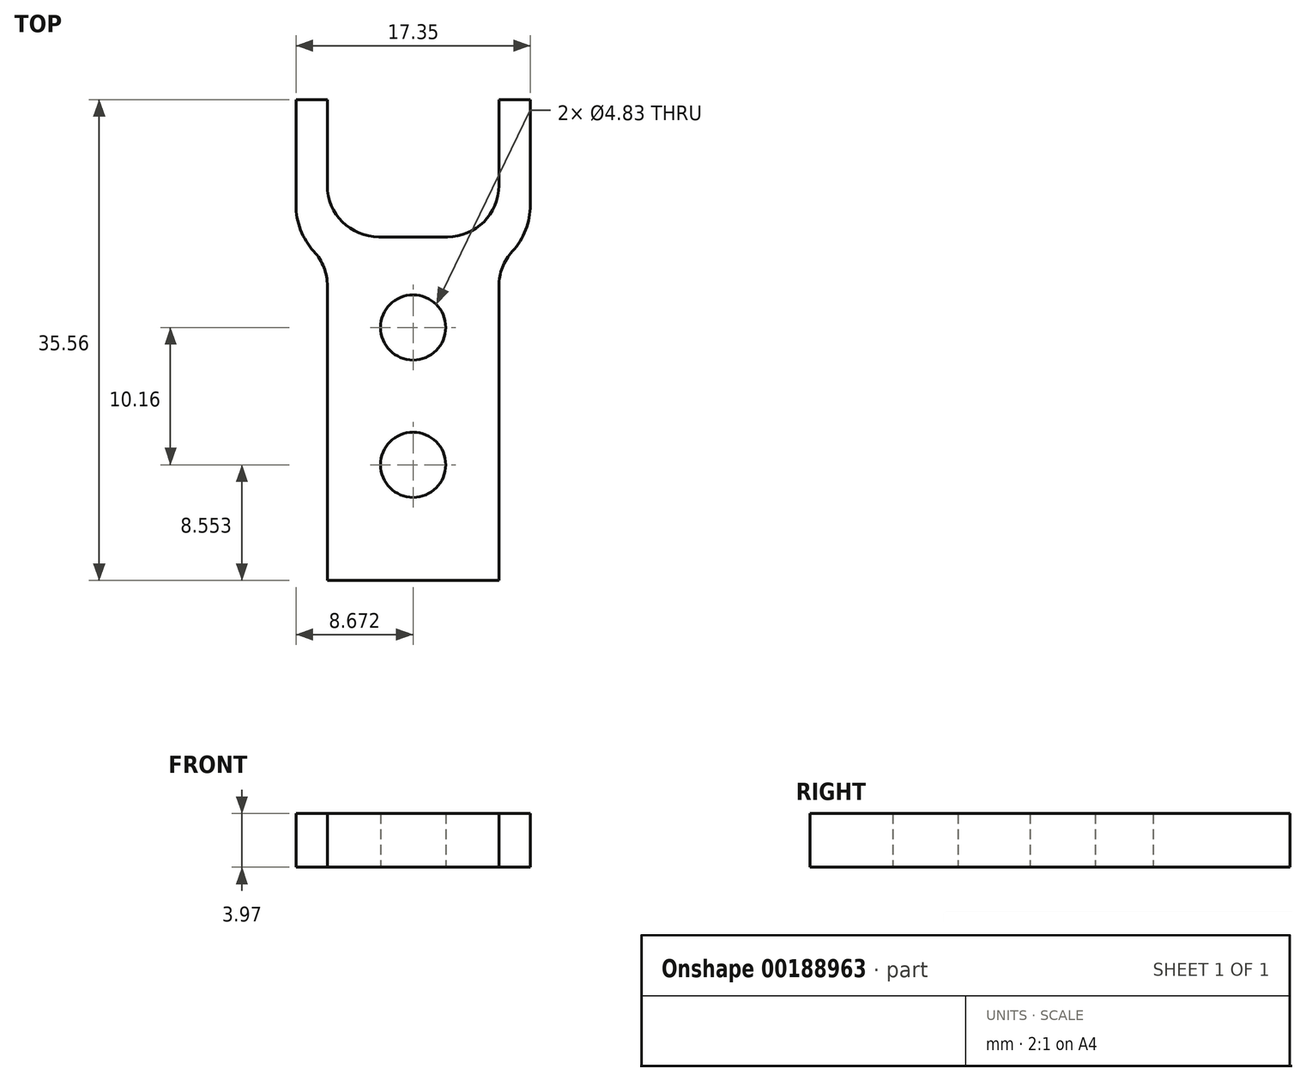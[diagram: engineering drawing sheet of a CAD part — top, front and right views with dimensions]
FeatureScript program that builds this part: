
annotation { "Feature Type Name" : "Feature", "Feature Type Description" : "" }
export const myFeature = defineFeature(function(context is Context, id is Id, definition is map)
    precondition{}
    {
        {
            var Q0;
            Q0=qCreatedBy(makeId("Top.planeOp"),FACE);
            var sketch = newSketch(context, id + "F0", { "sketchPlane" : qUnion([Q0])});
            skCircle(sketch, "E0", {"center": v(-68.64, 47.74) * mm, "radius": 6.88 * mm, "construction": true});
            skLineSegment(sketch, "E1", {"start": v(-68.64, 54.62) * mm, "end": v(-75.52, 47.74) * mm, "construction": true});
            skLineSegment(sketch, "E2", {"start": v(-75.52, 47.74) * mm, "end": v(-75.52, 54.62) * mm, "construction": true});
            skLineSegment(sketch, "E3", {"start": v(-75.52, 54.62) * mm, "end": v(-68.64, 54.62) * mm, "construction": true});
            skLineSegment(sketch, "E4", {"start": v(-68.64, 54.62) * mm, "end": v(-61.77, 47.74) * mm, "construction": true});
            skLineSegment(sketch, "E5", {"start": v(-61.77, 47.74) * mm, "end": v(-61.77, 54.62) * mm, "construction": true});
            skLineSegment(sketch, "E6", {"start": v(-61.77, 54.62) * mm, "end": v(-68.64, 54.62) * mm, "construction": true});
            skLineSegment(sketch, "E7.bottom", {"start": v(-75.88, 33.2) * mm, "end": v(-63.18, 33.2) * mm});
            skLineSegment(sketch, "E7.top", {"start": v(-75.88, 7.8) * mm, "end": v(-63.18, 7.8) * mm});
            skLineSegment(sketch, "E7.left", {"start": v(-75.88, 31.52) * mm, "end": v(-75.88, 7.8) * mm});
            skLineSegment(sketch, "E7.right", {"start": v(-63.18, 31.52) * mm, "end": v(-63.18, 7.8) * mm});
            skCircle(sketch, "E8", {"center": v(-69.53, 26.51) * mm, "radius": 2.41 * mm});
            skPoint(sketch, "E8.centerSnap0", {"position": v(-69.53, 33.2) * mm});
            skCircle(sketch, "E9", {"center": v(-69.53, 16.35) * mm, "radius": 2.41 * mm});
            skLineSegment(sketch, "E10", {"start": v(-78.2, 33.2) * mm, "end": v(-78.2, 43.36) * mm});
            skLineSegment(sketch, "E11", {"start": v(-78.2, 43.36) * mm, "end": v(-75.88, 43.36) * mm});
            skLineSegment(sketch, "E12", {"start": v(-75.88, 33.2) * mm, "end": v(-75.88, 43.36) * mm});
            skLineSegment(sketch, "E13", {"start": v(-60.85, 33.2) * mm, "end": v(-60.85, 43.36) * mm});
            skLineSegment(sketch, "E14", {"start": v(-60.85, 43.36) * mm, "end": v(-63.18, 43.36) * mm});
            skLineSegment(sketch, "E15", {"start": v(-63.18, 33.2) * mm, "end": v(-63.18, 43.36) * mm});
            skLineSegment(sketch, "E16", {"start": v(-78.2, 33.2) * mm, "end": v(-75.88, 31.52) * mm});
            skLineSegment(sketch, "E17", {"start": v(-60.85, 33.2) * mm, "end": v(-63.18, 31.52) * mm});
            skLineSegment(sketch, "E18", {"start": v(-75.88, 33.2) * mm, "end": v(-75.88, 31.52) * mm, "construction": true});
            skLineSegment(sketch, "E19", {"start": v(-63.18, 33.2) * mm, "end": v(-63.18, 31.52) * mm, "construction": true});
            skSolve(sketch);
        }
        {
            var Q0;
            Q0 = qSketchRegion(id + "F0", true);
            extrude(context, id + "F1", {"entities" : qUnion([Q0]), "depth" : 3.97 * mm});
        }
        {
            var Q0;
            Q0=makeQuery(id+"F1.opExtrude","SWEPT_EDGE",EDGE,{"disambiguationData":[OSD([sQuery(id+"F0.wireOp",EDGE,"E7.right"),sQuery(id+"F0.wireOp",EDGE,"E17")])]});
            var Q1;
            Q1=makeQuery(id+"F1.opExtrude","SWEPT_EDGE",EDGE,{"disambiguationData":[OSD([sQuery(id+"F0.wireOp",EDGE,"E7.left"),sQuery(id+"F0.wireOp",EDGE,"E16")])]});
            var Q2;
            Q2=makeQuery(id+"F1.opExtrude","SWEPT_EDGE",EDGE,{"disambiguationData":[OSD([sQuery(id+"F0.wireOp",EDGE,"E7.bottom"),sQuery(id+"F0.wireOp",EDGE,"E15")])]});
            var Q3;
            Q3=makeQuery(id+"F1.opExtrude","SWEPT_EDGE",EDGE,{"disambiguationData":[OSD([sQuery(id+"F0.wireOp",EDGE,"E7.bottom"),sQuery(id+"F0.wireOp",EDGE,"E12")])]});
            fillet(context, id + "F2", {"entities" : qUnion([Q0, Q1, Q2, Q3]), "radius" : 3.8 * mm, "tangentPropagation" : true, "allowEdgeOverflow" : false});
        }
        {
            var Q0;
            Q0=makeQuery(id+"F1.opExtrude","SWEPT_EDGE",EDGE,{"disambiguationData":[OSD([sQuery(id+"F0.wireOp",EDGE,"E10"),sQuery(id+"F0.wireOp",EDGE,"E16")])]});
            var Q1;
            Q1=makeQuery(id+"F1.opExtrude","SWEPT_EDGE",EDGE,{"disambiguationData":[OSD([sQuery(id+"F0.wireOp",EDGE,"E13"),sQuery(id+"F0.wireOp",EDGE,"E17")])]});
            fillet(context, id + "F3", {"entities" : qUnion([Q0, Q1]), "radius" : 5.08 * mm, "tangentPropagation" : true, "allowEdgeOverflow" : false});
        }
    });
